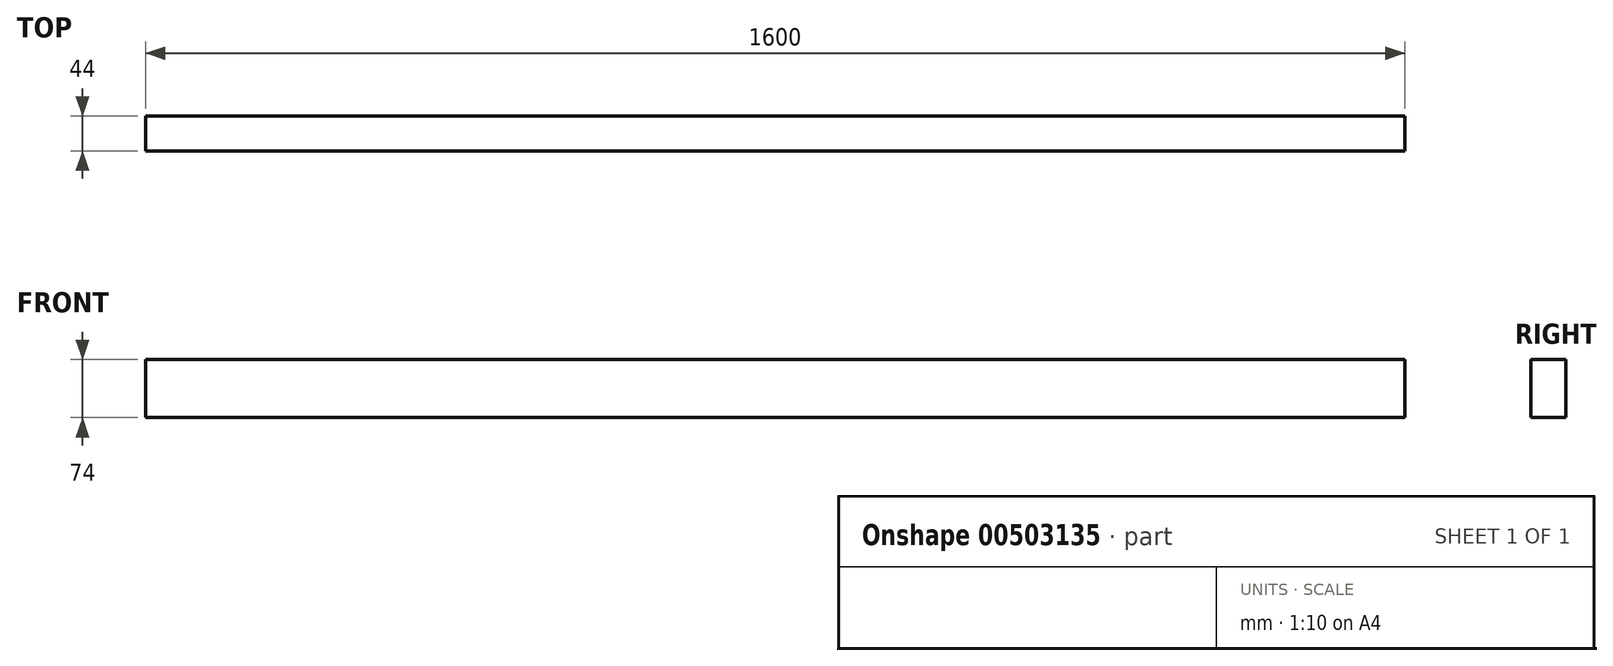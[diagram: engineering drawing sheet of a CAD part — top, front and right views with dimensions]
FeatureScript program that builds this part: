
annotation { "Feature Type Name" : "Feature", "Feature Type Description" : "" }
export const myFeature = defineFeature(function(context is Context, id is Id, definition is map)
    precondition{}
    {
        {
            var Q0;
            Q0=qCreatedBy(makeId("Front.planeOp"),FACE);
            var sketch = newSketch(context, id + "F0", { "sketchPlane" : qUnion([Q0])});
            skLineSegment(sketch, "E0.bottom", {"start": v(-410.5, 34.9) * mm, "end": v(1189.5, 34.9) * mm});
            skLineSegment(sketch, "E0.top", {"start": v(-410.5, -39.1) * mm, "end": v(1189.5, -39.1) * mm});
            skLineSegment(sketch, "E0.left", {"start": v(-410.5, 34.9) * mm, "end": v(-410.5, -39.1) * mm});
            skLineSegment(sketch, "E0.right", {"start": v(1189.5, 34.9) * mm, "end": v(1189.5, -39.1) * mm});
            skSolve(sketch);
        }
        {
            var Q0;
            Q0=makeQuery(id+"F0.imprint","IMPRINT",FACE,{"disambiguationData":[TD([[makeQuery(id+"F0.imprint","IMPRINT",EDGE,{"derivedFrom":sQuery(id+"F0.wireOp",EDGE,"E0.bottom")}),-1.0]])]});
            extrude(context, id + "F1", {"entities" : qUnion([Q0]), "depth" : 44 * mm, "offsetDistance" : 25 * mm});
        }
    });
